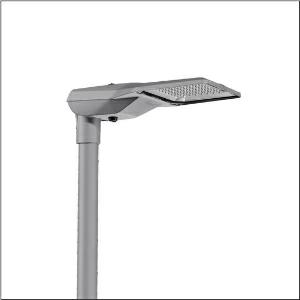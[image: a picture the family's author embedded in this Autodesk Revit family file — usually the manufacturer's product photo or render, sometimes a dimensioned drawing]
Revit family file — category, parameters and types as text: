
# Revit family: streetlight_sl_21_iq_midi___st1_0a_5xe3d21y08nb_2a15
name_source: partatom
category: Lighting Fixtures
units: mm (PartAtom-declared; Revit-internal decimal feet)

## family parameters
Cut with Voids When Loaded = No
Host = Face
Light Source = No
Part Type = Normal
Room Calculation Point = No
Round Connector Dimension = Use Diameter
Shared = No

## types (1)
- --- (1 x LED, 17280 lm, 136.6 W, 2200K)
    Apparent Load = 137 VA
    CIE Flux Codes = 40 73 97 100 100
    Color Rendering = 70
    Color Temperature = 2200K
    Default Elevation = 1800 mm
    Description = Streetlight SL 21 iQ midi, mast luminaire, primary light control with lens, of PMMA, primary optical cover: cover, of toughened safety glass, transparent, light distribution: ST1.0a, light emission: direct distribution, primary light characteristic: asymmetric, installation type: post-top, side-entry, LED, High Power LED, rated luminous flux: 17.280lm, luminous efficacy: 127lm/W, light colour: 722, colour temperature: 2200K, control: presetting dimming logarithmic, Street-Remote, Auto-Match, Temp-Guard, Lumen-Switch, Night-Set, Smart-Wire, Light-Fading, Desk-Remote (wireless, voltage-free reading and setting of iQ features in the workshop via application-optimized NFC function/RFID function), optimised constant luminous flux control (CLO 2.0), mains connection: 230..240V, AC, 50/60Hz, start of lifetime: 137W, end of service life: 144W, reduction: 61W, luminaire housing, of diecast aluminium, powder-coated, Siteco® metallic grey (DB 702S), corrosivity category C5 mid according to DIN EN ISO 12944, please order mast flange separately, inclination adjustable: 0°, 5°, 10°, 15°, sealing non-destructively replaceable, multi-level sealing system, length: 644mm, width: 335mm, height: 110mm, mast flange for spigot size: 42mm (side-entry): 5XC10008XM4, 60/48mm (side-entry/post-top): 5XC10108XM2, 76/60mm (side-entry/post-top): 5XC10108XM1, Smart Interface below and above, protection rating (complete): IP66, insulation class (complete): insulation class II (safety insulation), certification: CE, ENEC, ENEC+, VDE, impact resistance: IK09, permissible operating ambient temperature for outdoor applications: -40..+50°C, standard-compliant lighting for roads and squares, packaging unit: 1 piece

Light Distribution: ST1.0a
    Height = 111 mm
    Lamp = 1 x LED
    Lamp Light Flux = 17280 lm
    Lamp Power = 136.6 W
    Lamp count = 1
    Length = 644 mm
    Luminous efficacy = 127 lm/W
    Manufacturer = Siteco
    ModVariant = No
    Model = 5XE3D21Y08NB
    Number of Poles = 1
    OnlyDefault = Yes
    Power Factor = 1
    Product Name = Streetlight SL 21 iQ midi | ST1.0a
    Product group = mast luminaire | pylon top
    ProductGroupID = 6100
    Protection Class = Protection class II
    Protection Degree = IP 66
    RLX_Detail_Level = 1
    RLX_Emergency_Light_Flux = 0 lm
    RLX_Emergency_Type = 0
    RLX_Emergency_Type_DB = No
    RlxData = <blob elided: 90765 chars, md5=fffaf0c7>
    Socket = socket
    Standby Power = 0 W
    System Light Flux = 17280 lm
    System Power = 137 W
    Type Comments = factory setting: luminous flux: 100 % | dim-lin: 254 | 733 mA
    Type Image = l_1004304.jpg
    URL = http://relux.com
    VarID = @adj_043921
    Voltage = 0 V
    Weight = 0.00 kg
    Width = 336 mm

## geometry (parser evidence)
native form markers: Blend x4, Sweep x12
no freeform markers — native parametric forms only
